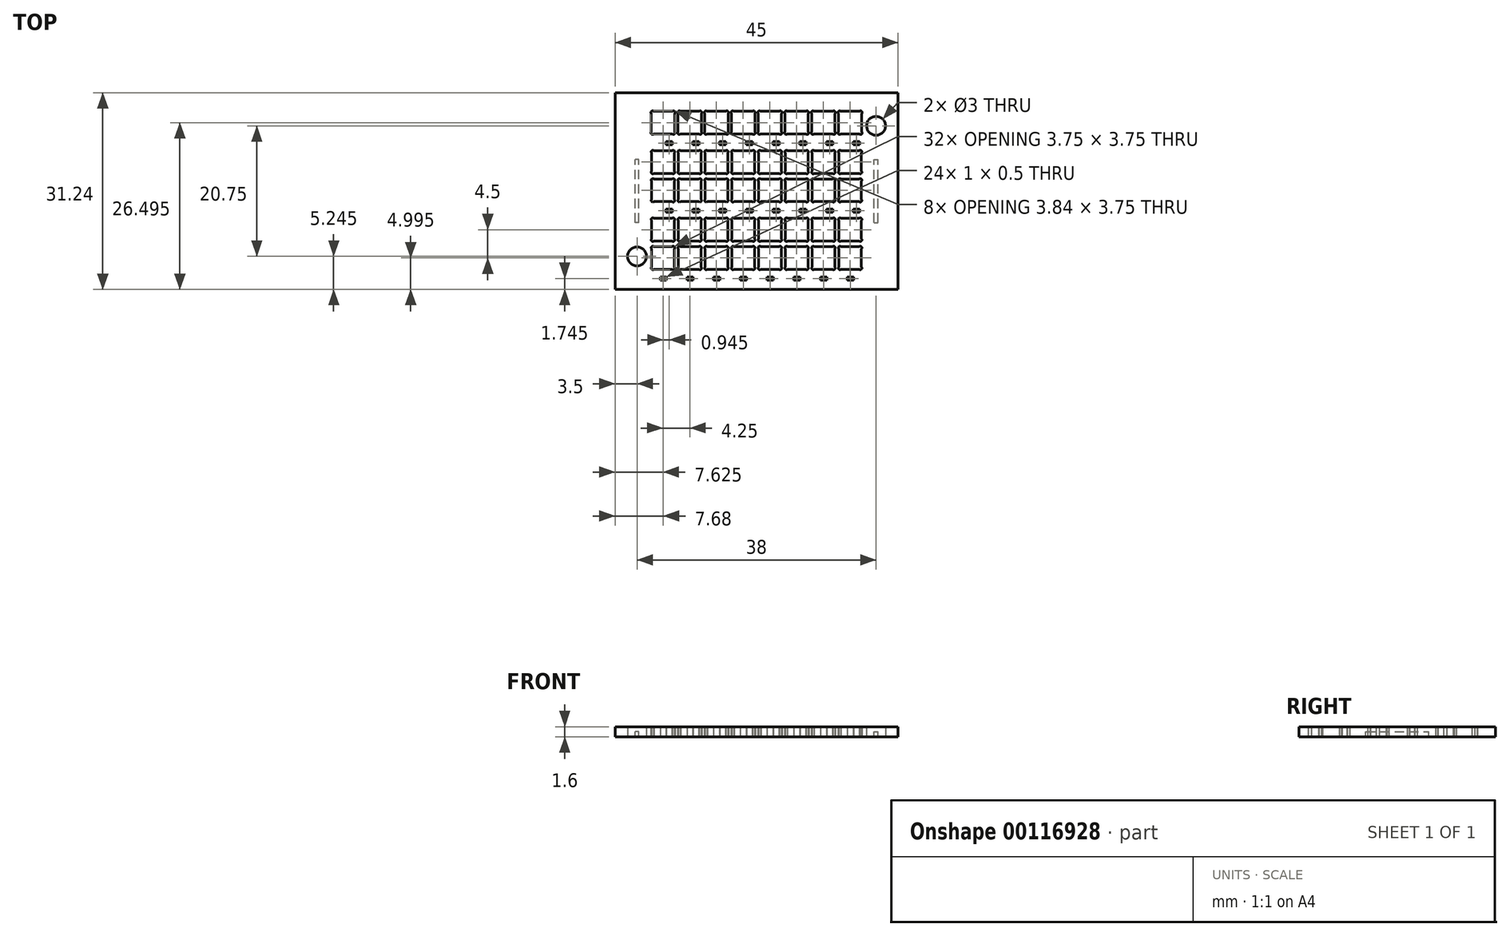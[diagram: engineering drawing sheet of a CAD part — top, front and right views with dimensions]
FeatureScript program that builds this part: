
annotation { "Feature Type Name" : "Feature", "Feature Type Description" : "" }
export const myFeature = defineFeature(function(context is Context, id is Id, definition is map)
    precondition{}
    {
        {
            var Q0;
            Q0=qCreatedBy(makeId("Top.planeOp"),FACE);
            var sketch = newSketch(context, id + "F0", { "sketchPlane" : qUnion([Q0])});
            skLineSegment(sketch, "E0.bottom", {"start": v(-13.38, 9.08) * mm, "end": v(-16.37, 9.08) * mm});
            skLineSegment(sketch, "E0.top", {"start": v(-13.38, 12.68) * mm, "end": v(-16.37, 12.68) * mm});
            skLineSegment(sketch, "E0.left", {"start": v(-13.03, 9.42) * mm, "end": v(-13.03, 12.33) * mm});
            skLineSegment(sketch, "E0.right", {"start": v(-16.73, 9.42) * mm, "end": v(-16.73, 12.33) * mm});
            skPoint(sketch, "E0.middle", {"position": v(-14.88, 10.88) * mm});
            skArc(sketch, "E1", {"start": v(-16.37, 12.68) * mm, "mid": v(-16.72, 12.68) * mm, "end": v(-16.73, 12.33) * mm});
            skLineSegment(sketch, "E2", {"start": v(-16.73, 12.68) * mm, "end": v(-14.88, 10.88) * mm, "construction": true});
            skLineSegment(sketch, "E3", {"start": v(-14.88, 12.68) * mm, "end": v(-14.88, 9.08) * mm, "construction": true});
            skLineSegment(sketch, "E4", {"start": v(-16.73, 10.88) * mm, "end": v(-13.03, 10.88) * mm, "construction": true});
            skArc(sketch, "E5.MirrorC", {"start": v(-16.37, 9.07) * mm, "mid": v(-16.72, 9.07) * mm, "end": v(-16.73, 9.42) * mm});
            skArc(sketch, "E6.MirrorC", {"start": v(-13.38, 12.68) * mm, "mid": v(-13.03, 12.68) * mm, "end": v(-13.03, 12.33) * mm});
            skArc(sketch, "E7.MirrorC", {"start": v(-13.38, 9.07) * mm, "mid": v(-13.03, 9.07) * mm, "end": v(-13.03, 9.42) * mm});
            skPoint(sketch, "E8.orphan", {"position": v(-13.03, 12.68) * mm});
            skPoint(sketch, "E9.orphan", {"position": v(-13.03, 9.07) * mm});
            skPoint(sketch, "E10.orphan", {"position": v(-16.73, 9.07) * mm});
            skLineSegment(sketch, "E11.1.0.0", {"start": v(-8.78, 9.42) * mm, "end": v(-8.78, 12.33) * mm});
            skArc(sketch, "E11.1.0.1", {"start": v(-9.13, 9.07) * mm, "mid": v(-8.78, 9.07) * mm, "end": v(-8.78, 9.42) * mm});
            skLineSegment(sketch, "E11.1.0.2", {"start": v(-9.13, 9.08) * mm, "end": v(-12.12, 9.08) * mm});
            skArc(sketch, "E11.1.0.3", {"start": v(-12.12, 9.07) * mm, "mid": v(-12.47, 9.07) * mm, "end": v(-12.48, 9.42) * mm});
            skLineSegment(sketch, "E11.1.0.4", {"start": v(-12.47, 9.42) * mm, "end": v(-12.47, 12.33) * mm});
            skArc(sketch, "E11.1.0.5", {"start": v(-12.12, 12.68) * mm, "mid": v(-12.47, 12.68) * mm, "end": v(-12.48, 12.33) * mm});
            skLineSegment(sketch, "E11.1.0.6", {"start": v(-9.13, 12.68) * mm, "end": v(-12.12, 12.68) * mm});
            skArc(sketch, "E11.1.0.7", {"start": v(-9.13, 12.68) * mm, "mid": v(-8.78, 12.68) * mm, "end": v(-8.78, 12.33) * mm});
            skLineSegment(sketch, "E11.2.0.0", {"start": v(-4.53, 9.42) * mm, "end": v(-4.53, 12.33) * mm});
            skArc(sketch, "E11.2.0.1", {"start": v(-4.88, 9.07) * mm, "mid": v(-4.53, 9.07) * mm, "end": v(-4.53, 9.42) * mm});
            skLineSegment(sketch, "E11.2.0.2", {"start": v(-4.88, 9.08) * mm, "end": v(-7.87, 9.08) * mm});
            skArc(sketch, "E11.2.0.3", {"start": v(-7.87, 9.07) * mm, "mid": v(-8.22, 9.07) * mm, "end": v(-8.23, 9.42) * mm});
            skLineSegment(sketch, "E11.2.0.4", {"start": v(-8.22, 9.42) * mm, "end": v(-8.22, 12.33) * mm});
            skArc(sketch, "E11.2.0.5", {"start": v(-7.87, 12.68) * mm, "mid": v(-8.22, 12.68) * mm, "end": v(-8.23, 12.33) * mm});
            skLineSegment(sketch, "E11.2.0.6", {"start": v(-4.88, 12.68) * mm, "end": v(-7.87, 12.68) * mm});
            skArc(sketch, "E11.2.0.7", {"start": v(-4.88, 12.68) * mm, "mid": v(-4.53, 12.68) * mm, "end": v(-4.53, 12.33) * mm});
            skLineSegment(sketch, "E11.3.0.0", {"start": v(-0.28, 9.42) * mm, "end": v(-0.28, 12.33) * mm});
            skArc(sketch, "E11.3.0.1", {"start": v(-0.63, 9.07) * mm, "mid": v(-0.28, 9.07) * mm, "end": v(-0.28, 9.42) * mm});
            skLineSegment(sketch, "E11.3.0.2", {"start": v(-0.63, 9.08) * mm, "end": v(-3.62, 9.08) * mm});
            skArc(sketch, "E11.3.0.3", {"start": v(-3.62, 9.07) * mm, "mid": v(-3.97, 9.07) * mm, "end": v(-3.98, 9.42) * mm});
            skLineSegment(sketch, "E11.3.0.4", {"start": v(-3.97, 9.42) * mm, "end": v(-3.97, 12.33) * mm});
            skArc(sketch, "E11.3.0.5", {"start": v(-3.62, 12.68) * mm, "mid": v(-3.97, 12.68) * mm, "end": v(-3.98, 12.33) * mm});
            skLineSegment(sketch, "E11.3.0.6", {"start": v(-0.63, 12.68) * mm, "end": v(-3.62, 12.68) * mm});
            skArc(sketch, "E11.3.0.7", {"start": v(-0.63, 12.68) * mm, "mid": v(-0.28, 12.68) * mm, "end": v(-0.28, 12.33) * mm});
            skLineSegment(sketch, "E11.4.0.0", {"start": v(3.97, 9.42) * mm, "end": v(3.97, 12.33) * mm});
            skArc(sketch, "E11.4.0.1", {"start": v(3.62, 9.07) * mm, "mid": v(3.97, 9.07) * mm, "end": v(3.97, 9.42) * mm});
            skLineSegment(sketch, "E11.4.0.2", {"start": v(3.62, 9.08) * mm, "end": v(0.63, 9.08) * mm});
            skArc(sketch, "E11.4.0.3", {"start": v(0.63, 9.07) * mm, "mid": v(0.28, 9.07) * mm, "end": v(0.27, 9.42) * mm});
            skLineSegment(sketch, "E11.4.0.4", {"start": v(0.28, 9.42) * mm, "end": v(0.28, 12.33) * mm});
            skArc(sketch, "E11.4.0.5", {"start": v(0.63, 12.68) * mm, "mid": v(0.28, 12.68) * mm, "end": v(0.27, 12.33) * mm});
            skLineSegment(sketch, "E11.4.0.6", {"start": v(3.62, 12.68) * mm, "end": v(0.63, 12.68) * mm});
            skArc(sketch, "E11.4.0.7", {"start": v(3.62, 12.68) * mm, "mid": v(3.97, 12.68) * mm, "end": v(3.97, 12.33) * mm});
            skLineSegment(sketch, "E11.5.0.0", {"start": v(8.22, 9.42) * mm, "end": v(8.22, 12.33) * mm});
            skArc(sketch, "E11.5.0.1", {"start": v(7.87, 9.07) * mm, "mid": v(8.22, 9.07) * mm, "end": v(8.22, 9.42) * mm});
            skLineSegment(sketch, "E11.5.0.2", {"start": v(7.87, 9.08) * mm, "end": v(4.88, 9.08) * mm});
            skArc(sketch, "E11.5.0.3", {"start": v(4.88, 9.07) * mm, "mid": v(4.53, 9.07) * mm, "end": v(4.52, 9.42) * mm});
            skLineSegment(sketch, "E11.5.0.4", {"start": v(4.53, 9.42) * mm, "end": v(4.53, 12.33) * mm});
            skArc(sketch, "E11.5.0.5", {"start": v(4.88, 12.68) * mm, "mid": v(4.53, 12.68) * mm, "end": v(4.52, 12.33) * mm});
            skLineSegment(sketch, "E11.5.0.6", {"start": v(7.87, 12.68) * mm, "end": v(4.88, 12.68) * mm});
            skArc(sketch, "E11.5.0.7", {"start": v(7.87, 12.68) * mm, "mid": v(8.22, 12.68) * mm, "end": v(8.22, 12.33) * mm});
            skLineSegment(sketch, "E11.6.0.0", {"start": v(12.47, 9.42) * mm, "end": v(12.47, 12.33) * mm});
            skArc(sketch, "E11.6.0.1", {"start": v(12.12, 9.07) * mm, "mid": v(12.47, 9.07) * mm, "end": v(12.47, 9.42) * mm});
            skLineSegment(sketch, "E11.6.0.2", {"start": v(12.12, 9.08) * mm, "end": v(9.13, 9.08) * mm});
            skArc(sketch, "E11.6.0.3", {"start": v(9.13, 9.07) * mm, "mid": v(8.78, 9.07) * mm, "end": v(8.77, 9.42) * mm});
            skLineSegment(sketch, "E11.6.0.4", {"start": v(8.78, 9.42) * mm, "end": v(8.78, 12.33) * mm});
            skArc(sketch, "E11.6.0.5", {"start": v(9.13, 12.68) * mm, "mid": v(8.78, 12.68) * mm, "end": v(8.77, 12.33) * mm});
            skLineSegment(sketch, "E11.6.0.6", {"start": v(12.12, 12.68) * mm, "end": v(9.13, 12.68) * mm});
            skArc(sketch, "E11.6.0.7", {"start": v(12.12, 12.68) * mm, "mid": v(12.47, 12.68) * mm, "end": v(12.47, 12.33) * mm});
            skLineSegment(sketch, "E11.7.0.0", {"start": v(16.73, 9.42) * mm, "end": v(16.73, 12.33) * mm});
            skArc(sketch, "E11.7.0.1", {"start": v(16.37, 9.07) * mm, "mid": v(16.72, 9.07) * mm, "end": v(16.73, 9.42) * mm});
            skLineSegment(sketch, "E11.7.0.2", {"start": v(16.37, 9.08) * mm, "end": v(13.38, 9.08) * mm});
            skArc(sketch, "E11.7.0.3", {"start": v(13.38, 9.08) * mm, "mid": v(13.03, 9.07) * mm, "end": v(13.02, 9.42) * mm});
            skLineSegment(sketch, "E11.7.0.4", {"start": v(13.03, 9.42) * mm, "end": v(13.03, 12.33) * mm});
            skArc(sketch, "E11.7.0.5", {"start": v(13.38, 12.68) * mm, "mid": v(13.03, 12.68) * mm, "end": v(13.02, 12.33) * mm});
            skLineSegment(sketch, "E11.7.0.6", {"start": v(16.37, 12.68) * mm, "end": v(13.38, 12.68) * mm});
            skArc(sketch, "E11.7.0.7", {"start": v(16.37, 12.68) * mm, "mid": v(16.72, 12.68) * mm, "end": v(16.73, 12.33) * mm});
            skLineSegment(sketch, "E11.direction1", {"start": v(-13.03, 9.42) * mm, "end": v(-8.78, 9.42) * mm, "construction": true});
            skLineSegment(sketch, "E12", {"start": v(-16.73, 10.87) * mm, "end": v(16.73, 10.88) * mm, "construction": true});
            skPoint(sketch, "E13", {"position": v(0, 10.87) * mm});
            skCircle(sketch, "E14", {"center": v(-19, 10.38) * mm, "radius": 1.5 * mm});
            skCircle(sketch, "E15.MirrorC", {"center": v(19, 10.38) * mm, "radius": 1.5 * mm});
            skCircle(sketch, "E16.MirrorC", {"center": v(-19, -10.38) * mm, "radius": 1.5 * mm});
            skCircle(sketch, "E17.MirrorC", {"center": v(19, -10.38) * mm, "radius": 1.5 * mm});
            skLineSegment(sketch, "E18.0.1.0", {"start": v(8.17, -1.32) * mm, "end": v(8.17, 1.57) * mm});
            skLineSegment(sketch, "E18.0.1.1", {"start": v(-0.68, -1.68) * mm, "end": v(-3.57, -1.68) * mm});
            skLineSegment(sketch, "E18.0.1.2", {"start": v(7.82, -1.68) * mm, "end": v(4.93, -1.68) * mm});
            skLineSegment(sketch, "E18.0.1.3", {"start": v(16.32, -1.68) * mm, "end": v(13.43, -1.68) * mm});
            skPoint(sketch, "E18.0.1.5", {"position": v(0, 0.12) * mm});
            skLineSegment(sketch, "E18.0.1.6", {"start": v(-4.93, -1.68) * mm, "end": v(-7.82, -1.68) * mm});
            skLineSegment(sketch, "E18.0.1.7", {"start": v(12.07, -1.68) * mm, "end": v(9.18, -1.68) * mm});
            skLineSegment(sketch, "E18.0.1.8", {"start": v(3.57, -1.68) * mm, "end": v(0.68, -1.68) * mm});
            skPoint(sketch, "E18.0.1.9", {"position": v(-13.07, 1.93) * mm});
            skLineSegment(sketch, "E18.0.1.10", {"start": v(4.57, -1.32) * mm, "end": v(4.57, 1.57) * mm});
            skLineSegment(sketch, "E18.0.1.11", {"start": v(13.07, -1.32) * mm, "end": v(13.07, 1.57) * mm});
            skLineSegment(sketch, "E18.0.1.12", {"start": v(-3.93, -1.32) * mm, "end": v(-3.93, 1.57) * mm});
            skLineSegment(sketch, "E18.0.1.13", {"start": v(-9.18, -1.68) * mm, "end": v(-12.07, -1.68) * mm});
            skLineSegment(sketch, "E18.0.1.14", {"start": v(-8.83, -1.32) * mm, "end": v(-8.83, 1.57) * mm});
            skLineSegment(sketch, "E18.0.1.15", {"start": v(8.82, -1.32) * mm, "end": v(8.82, 1.57) * mm});
            skLineSegment(sketch, "E18.0.1.16", {"start": v(-8.18, -1.32) * mm, "end": v(-8.18, 1.57) * mm});
            skPoint(sketch, "E18.0.1.17", {"position": v(-13.07, -1.68) * mm});
            skPoint(sketch, "E18.0.1.18", {"position": v(-16.68, -1.67) * mm});
            skLineSegment(sketch, "E18.0.1.19", {"start": v(-9.18, 1.92) * mm, "end": v(-12.07, 1.92) * mm});
            skLineSegment(sketch, "E18.0.1.20", {"start": v(16.32, 1.92) * mm, "end": v(13.43, 1.92) * mm});
            skLineSegment(sketch, "E18.0.1.21", {"start": v(7.82, 1.92) * mm, "end": v(4.93, 1.92) * mm});
            skLineSegment(sketch, "E18.0.1.22", {"start": v(-0.68, 1.92) * mm, "end": v(-3.57, 1.92) * mm});
            skLineSegment(sketch, "E18.0.1.23", {"start": v(12.07, 1.92) * mm, "end": v(9.18, 1.92) * mm});
            skLineSegment(sketch, "E18.0.1.24", {"start": v(3.57, 1.92) * mm, "end": v(0.68, 1.92) * mm});
            skLineSegment(sketch, "E18.0.1.25", {"start": v(-4.93, 1.92) * mm, "end": v(-7.82, 1.92) * mm});
            skPoint(sketch, "E18.0.1.26", {"position": v(-14.88, 0.13) * mm});
            skLineSegment(sketch, "E18.0.1.27", {"start": v(3.92, -1.32) * mm, "end": v(3.92, 1.57) * mm});
            skLineSegment(sketch, "E18.0.1.28", {"start": v(12.42, -1.32) * mm, "end": v(12.42, 1.57) * mm});
            skLineSegment(sketch, "E18.0.1.30", {"start": v(-4.58, -1.32) * mm, "end": v(-4.58, 1.57) * mm});
            skLineSegment(sketch, "E18.0.1.31", {"start": v(-0.33, -1.32) * mm, "end": v(-0.33, 1.57) * mm});
            skLineSegment(sketch, "E18.0.1.32", {"start": v(16.68, -1.32) * mm, "end": v(16.68, 1.57) * mm});
            skLineSegment(sketch, "E18.0.1.34", {"start": v(-12.43, -1.32) * mm, "end": v(-12.43, 1.57) * mm});
            skLineSegment(sketch, "E18.0.1.35", {"start": v(-13.43, -1.68) * mm, "end": v(-16.32, -1.68) * mm});
            skLineSegment(sketch, "E18.0.1.36", {"start": v(-13.08, -1.32) * mm, "end": v(-13.08, 1.57) * mm});
            skLineSegment(sketch, "E18.0.1.39", {"start": v(0.32, -1.32) * mm, "end": v(0.32, 1.57) * mm});
            skArc(sketch, "E18.0.1.40", {"start": v(3.57, -1.68) * mm, "mid": v(3.92, -1.68) * mm, "end": v(3.92, -1.32) * mm});
            skArc(sketch, "E18.0.1.41", {"start": v(12.07, 1.92) * mm, "mid": v(12.42, 1.92) * mm, "end": v(12.42, 1.57) * mm});
            skArc(sketch, "E18.0.1.42", {"start": v(16.32, -1.68) * mm, "mid": v(16.67, -1.68) * mm, "end": v(16.67, -1.32) * mm});
            skArc(sketch, "E18.0.1.43", {"start": v(7.82, -1.68) * mm, "mid": v(8.17, -1.68) * mm, "end": v(8.17, -1.32) * mm});
            skArc(sketch, "E18.0.1.44", {"start": v(13.43, -1.68) * mm, "mid": v(13.07, -1.68) * mm, "end": v(13.07, -1.32) * mm});
            skArc(sketch, "E18.0.1.45", {"start": v(-3.57, -1.68) * mm, "mid": v(-3.93, -1.67) * mm, "end": v(-3.93, -1.32) * mm});
            skArc(sketch, "E18.0.1.46", {"start": v(-4.93, 1.93) * mm, "mid": v(-4.57, 1.92) * mm, "end": v(-4.58, 1.57) * mm});
            skLineSegment(sketch, "E18.0.1.47", {"start": v(-13.43, 1.92) * mm, "end": v(-16.32, 1.92) * mm});
            skLineSegment(sketch, "E18.0.1.48", {"start": v(-16.68, -1.32) * mm, "end": v(-16.68, 1.57) * mm});
            skArc(sketch, "E18.0.1.50", {"start": v(0.68, 1.92) * mm, "mid": v(0.32, 1.92) * mm, "end": v(0.32, 1.57) * mm});
            skArc(sketch, "E18.0.1.51", {"start": v(-7.82, 1.93) * mm, "mid": v(-8.18, 1.92) * mm, "end": v(-8.18, 1.57) * mm});
            skArc(sketch, "E18.0.1.52", {"start": v(16.32, 1.92) * mm, "mid": v(16.67, 1.92) * mm, "end": v(16.67, 1.57) * mm});
            skArc(sketch, "E18.0.1.53", {"start": v(-4.93, -1.68) * mm, "mid": v(-4.57, -1.68) * mm, "end": v(-4.57, -1.32) * mm});
            skArc(sketch, "E18.0.1.54", {"start": v(12.07, -1.68) * mm, "mid": v(12.42, -1.68) * mm, "end": v(12.42, -1.32) * mm});
            skArc(sketch, "E18.0.1.55", {"start": v(-0.68, -1.68) * mm, "mid": v(-0.32, -1.67) * mm, "end": v(-0.32, -1.32) * mm});
            skArc(sketch, "E18.0.1.56", {"start": v(4.93, -1.68) * mm, "mid": v(4.57, -1.68) * mm, "end": v(4.57, -1.32) * mm});
            skArc(sketch, "E18.0.1.57", {"start": v(3.57, 1.92) * mm, "mid": v(3.93, 1.92) * mm, "end": v(3.92, 1.57) * mm});
            skArc(sketch, "E18.0.1.58", {"start": v(-7.82, -1.68) * mm, "mid": v(-8.18, -1.67) * mm, "end": v(-8.18, -1.32) * mm});
            skArc(sketch, "E18.0.1.59", {"start": v(9.18, -1.68) * mm, "mid": v(8.82, -1.68) * mm, "end": v(8.82, -1.32) * mm});
            skArc(sketch, "E18.0.1.60", {"start": v(0.68, -1.68) * mm, "mid": v(0.32, -1.68) * mm, "end": v(0.32, -1.32) * mm});
            skArc(sketch, "E18.0.1.61", {"start": v(-16.32, -1.68) * mm, "mid": v(-16.68, -1.67) * mm, "end": v(-16.68, -1.32) * mm});
            skArc(sketch, "E18.0.1.62", {"start": v(-9.18, -1.68) * mm, "mid": v(-8.82, -1.68) * mm, "end": v(-8.82, -1.32) * mm});
            skArc(sketch, "E18.0.1.63", {"start": v(7.82, 1.92) * mm, "mid": v(8.17, 1.92) * mm, "end": v(8.17, 1.57) * mm});
            skArc(sketch, "E18.0.1.64", {"start": v(-12.07, 1.93) * mm, "mid": v(-12.43, 1.92) * mm, "end": v(-12.43, 1.57) * mm});
            skArc(sketch, "E18.0.1.65", {"start": v(13.43, 1.92) * mm, "mid": v(13.07, 1.92) * mm, "end": v(13.07, 1.57) * mm});
            skArc(sketch, "E18.0.1.66", {"start": v(4.93, 1.92) * mm, "mid": v(4.57, 1.92) * mm, "end": v(4.57, 1.57) * mm});
            skArc(sketch, "E18.0.1.67", {"start": v(-3.57, 1.93) * mm, "mid": v(-3.93, 1.92) * mm, "end": v(-3.93, 1.57) * mm});
            skArc(sketch, "E18.0.1.68", {"start": v(9.18, 1.92) * mm, "mid": v(8.82, 1.92) * mm, "end": v(8.82, 1.57) * mm});
            skArc(sketch, "E18.0.1.69", {"start": v(-9.18, 1.93) * mm, "mid": v(-8.82, 1.92) * mm, "end": v(-8.82, 1.57) * mm});
            skArc(sketch, "E18.0.1.70", {"start": v(-12.07, -1.68) * mm, "mid": v(-12.43, -1.67) * mm, "end": v(-12.43, -1.32) * mm});
            skArc(sketch, "E18.0.1.71", {"start": v(-13.43, 1.93) * mm, "mid": v(-13.07, 1.92) * mm, "end": v(-13.07, 1.57) * mm});
            skArc(sketch, "E18.0.1.72", {"start": v(-13.43, -1.68) * mm, "mid": v(-13.07, -1.68) * mm, "end": v(-13.07, -1.32) * mm});
            skArc(sketch, "E18.0.1.73", {"start": v(-0.68, 1.93) * mm, "mid": v(-0.32, 1.92) * mm, "end": v(-0.33, 1.57) * mm});
            skArc(sketch, "E18.0.1.74", {"start": v(-16.32, 1.93) * mm, "mid": v(-16.68, 1.92) * mm, "end": v(-16.68, 1.57) * mm});
            skLineSegment(sketch, "E18.0.2.0", {"start": v(8.17, -12.07) * mm, "end": v(8.17, -9.18) * mm});
            skLineSegment(sketch, "E18.0.2.1", {"start": v(-0.68, -12.43) * mm, "end": v(-3.57, -12.43) * mm});
            skLineSegment(sketch, "E18.0.2.2", {"start": v(7.82, -12.43) * mm, "end": v(4.93, -12.43) * mm});
            skLineSegment(sketch, "E18.0.2.3", {"start": v(16.32, -12.43) * mm, "end": v(13.43, -12.43) * mm});
            skPoint(sketch, "E18.0.2.5", {"position": v(0, -10.63) * mm});
            skLineSegment(sketch, "E18.0.2.6", {"start": v(-4.93, -12.43) * mm, "end": v(-7.82, -12.43) * mm});
            skLineSegment(sketch, "E18.0.2.7", {"start": v(12.07, -12.43) * mm, "end": v(9.18, -12.43) * mm});
            skLineSegment(sketch, "E18.0.2.8", {"start": v(3.57, -12.43) * mm, "end": v(0.68, -12.43) * mm});
            skPoint(sketch, "E18.0.2.9", {"position": v(-13.07, -8.82) * mm});
            skLineSegment(sketch, "E18.0.2.10", {"start": v(4.57, -12.07) * mm, "end": v(4.57, -9.18) * mm});
            skLineSegment(sketch, "E18.0.2.11", {"start": v(13.07, -12.07) * mm, "end": v(13.07, -9.18) * mm});
            skLineSegment(sketch, "E18.0.2.12", {"start": v(-3.93, -12.07) * mm, "end": v(-3.93, -9.18) * mm});
            skLineSegment(sketch, "E18.0.2.13", {"start": v(-9.18, -12.43) * mm, "end": v(-12.07, -12.43) * mm});
            skLineSegment(sketch, "E18.0.2.14", {"start": v(-8.83, -12.07) * mm, "end": v(-8.83, -9.18) * mm});
            skLineSegment(sketch, "E18.0.2.15", {"start": v(8.82, -12.07) * mm, "end": v(8.82, -9.18) * mm});
            skLineSegment(sketch, "E18.0.2.16", {"start": v(-8.18, -12.07) * mm, "end": v(-8.18, -9.18) * mm});
            skPoint(sketch, "E18.0.2.17", {"position": v(-13.07, -12.43) * mm});
            skPoint(sketch, "E18.0.2.18", {"position": v(-16.68, -12.43) * mm});
            skLineSegment(sketch, "E18.0.2.19", {"start": v(-9.18, -8.83) * mm, "end": v(-12.07, -8.83) * mm});
            skLineSegment(sketch, "E18.0.2.20", {"start": v(16.32, -8.83) * mm, "end": v(13.43, -8.83) * mm});
            skLineSegment(sketch, "E18.0.2.21", {"start": v(7.82, -8.83) * mm, "end": v(4.93, -8.83) * mm});
            skLineSegment(sketch, "E18.0.2.22", {"start": v(-0.68, -8.83) * mm, "end": v(-3.57, -8.83) * mm});
            skLineSegment(sketch, "E18.0.2.23", {"start": v(12.07, -8.83) * mm, "end": v(9.18, -8.83) * mm});
            skLineSegment(sketch, "E18.0.2.24", {"start": v(3.57, -8.83) * mm, "end": v(0.68, -8.83) * mm});
            skLineSegment(sketch, "E18.0.2.25", {"start": v(-4.93, -8.83) * mm, "end": v(-7.82, -8.83) * mm});
            skPoint(sketch, "E18.0.2.26", {"position": v(-14.82, -9.25) * mm});
            skLineSegment(sketch, "E18.0.2.27", {"start": v(3.92, -12.07) * mm, "end": v(3.92, -9.18) * mm});
            skLineSegment(sketch, "E18.0.2.28", {"start": v(12.42, -12.07) * mm, "end": v(12.42, -9.18) * mm});
            skLineSegment(sketch, "E18.0.2.30", {"start": v(-4.58, -12.07) * mm, "end": v(-4.58, -9.18) * mm});
            skLineSegment(sketch, "E18.0.2.31", {"start": v(-0.33, -12.07) * mm, "end": v(-0.33, -9.18) * mm});
            skLineSegment(sketch, "E18.0.2.32", {"start": v(16.68, -12.07) * mm, "end": v(16.68, -9.18) * mm});
            skLineSegment(sketch, "E18.0.2.34", {"start": v(-12.43, -12.07) * mm, "end": v(-12.43, -9.18) * mm});
            skLineSegment(sketch, "E18.0.2.35", {"start": v(-13.43, -12.43) * mm, "end": v(-16.32, -12.43) * mm});
            skLineSegment(sketch, "E18.0.2.36", {"start": v(-13.08, -12.07) * mm, "end": v(-13.08, -9.18) * mm});
            skLineSegment(sketch, "E18.0.2.39", {"start": v(0.32, -12.07) * mm, "end": v(0.32, -9.18) * mm});
            skArc(sketch, "E18.0.2.40", {"start": v(3.57, -12.43) * mm, "mid": v(3.92, -12.43) * mm, "end": v(3.92, -12.07) * mm});
            skArc(sketch, "E18.0.2.41", {"start": v(12.07, -8.83) * mm, "mid": v(12.42, -8.83) * mm, "end": v(12.42, -9.18) * mm});
            skArc(sketch, "E18.0.2.42", {"start": v(16.32, -12.43) * mm, "mid": v(16.67, -12.43) * mm, "end": v(16.67, -12.07) * mm});
            skArc(sketch, "E18.0.2.43", {"start": v(7.82, -12.43) * mm, "mid": v(8.17, -12.43) * mm, "end": v(8.17, -12.07) * mm});
            skArc(sketch, "E18.0.2.44", {"start": v(13.43, -12.43) * mm, "mid": v(13.07, -12.43) * mm, "end": v(13.07, -12.07) * mm});
            skArc(sketch, "E18.0.2.45", {"start": v(-3.57, -12.43) * mm, "mid": v(-3.93, -12.43) * mm, "end": v(-3.93, -12.07) * mm});
            skArc(sketch, "E18.0.2.46", {"start": v(-4.93, -8.82) * mm, "mid": v(-4.57, -8.83) * mm, "end": v(-4.58, -9.18) * mm});
            skLineSegment(sketch, "E18.0.2.47", {"start": v(-13.43, -8.83) * mm, "end": v(-16.32, -8.83) * mm});
            skLineSegment(sketch, "E18.0.2.48", {"start": v(-16.68, -12.07) * mm, "end": v(-16.68, -9.18) * mm});
            skLineSegment(sketch, "E18.0.2.49", {"start": v(-16.62, -7.45) * mm, "end": v(-14.82, -9.25) * mm, "construction": true});
            skArc(sketch, "E18.0.2.50", {"start": v(0.68, -8.83) * mm, "mid": v(0.32, -8.83) * mm, "end": v(0.32, -9.18) * mm});
            skArc(sketch, "E18.0.2.51", {"start": v(-7.82, -8.82) * mm, "mid": v(-8.18, -8.83) * mm, "end": v(-8.18, -9.18) * mm});
            skArc(sketch, "E18.0.2.52", {"start": v(16.32, -8.83) * mm, "mid": v(16.67, -8.83) * mm, "end": v(16.67, -9.18) * mm});
            skArc(sketch, "E18.0.2.53", {"start": v(-4.93, -12.43) * mm, "mid": v(-4.57, -12.43) * mm, "end": v(-4.57, -12.07) * mm});
            skArc(sketch, "E18.0.2.54", {"start": v(12.07, -12.43) * mm, "mid": v(12.42, -12.43) * mm, "end": v(12.42, -12.07) * mm});
            skArc(sketch, "E18.0.2.55", {"start": v(-0.68, -12.43) * mm, "mid": v(-0.32, -12.43) * mm, "end": v(-0.32, -12.07) * mm});
            skArc(sketch, "E18.0.2.56", {"start": v(4.93, -12.43) * mm, "mid": v(4.57, -12.43) * mm, "end": v(4.57, -12.07) * mm});
            skArc(sketch, "E18.0.2.57", {"start": v(3.57, -8.83) * mm, "mid": v(3.93, -8.83) * mm, "end": v(3.92, -9.18) * mm});
            skArc(sketch, "E18.0.2.58", {"start": v(-7.82, -12.43) * mm, "mid": v(-8.18, -12.43) * mm, "end": v(-8.18, -12.07) * mm});
            skArc(sketch, "E18.0.2.59", {"start": v(9.18, -12.43) * mm, "mid": v(8.82, -12.43) * mm, "end": v(8.82, -12.07) * mm});
            skArc(sketch, "E18.0.2.60", {"start": v(0.68, -12.43) * mm, "mid": v(0.32, -12.43) * mm, "end": v(0.32, -12.07) * mm});
            skArc(sketch, "E18.0.2.61", {"start": v(-16.32, -12.43) * mm, "mid": v(-16.68, -12.43) * mm, "end": v(-16.68, -12.07) * mm});
            skArc(sketch, "E18.0.2.62", {"start": v(-9.18, -12.43) * mm, "mid": v(-8.82, -12.43) * mm, "end": v(-8.82, -12.07) * mm});
            skArc(sketch, "E18.0.2.63", {"start": v(7.82, -8.83) * mm, "mid": v(8.17, -8.83) * mm, "end": v(8.17, -9.18) * mm});
            skArc(sketch, "E18.0.2.64", {"start": v(-12.07, -8.82) * mm, "mid": v(-12.43, -8.83) * mm, "end": v(-12.43, -9.18) * mm});
            skArc(sketch, "E18.0.2.65", {"start": v(13.43, -8.83) * mm, "mid": v(13.07, -8.83) * mm, "end": v(13.07, -9.18) * mm});
            skArc(sketch, "E18.0.2.66", {"start": v(4.93, -8.83) * mm, "mid": v(4.57, -8.83) * mm, "end": v(4.57, -9.18) * mm});
            skArc(sketch, "E18.0.2.67", {"start": v(-3.57, -8.82) * mm, "mid": v(-3.93, -8.83) * mm, "end": v(-3.93, -9.18) * mm});
            skArc(sketch, "E18.0.2.68", {"start": v(9.18, -8.83) * mm, "mid": v(8.82, -8.83) * mm, "end": v(8.82, -9.18) * mm});
            skArc(sketch, "E18.0.2.69", {"start": v(-9.18, -8.82) * mm, "mid": v(-8.82, -8.83) * mm, "end": v(-8.82, -9.18) * mm});
            skArc(sketch, "E18.0.2.70", {"start": v(-12.07, -12.43) * mm, "mid": v(-12.43, -12.43) * mm, "end": v(-12.43, -12.07) * mm});
            skArc(sketch, "E18.0.2.71", {"start": v(-13.43, -8.82) * mm, "mid": v(-13.07, -8.83) * mm, "end": v(-13.07, -9.18) * mm});
            skArc(sketch, "E18.0.2.72", {"start": v(-13.43, -12.43) * mm, "mid": v(-13.07, -12.43) * mm, "end": v(-13.07, -12.07) * mm});
            skArc(sketch, "E18.0.2.73", {"start": v(-0.68, -8.82) * mm, "mid": v(-0.32, -8.83) * mm, "end": v(-0.33, -9.18) * mm});
            skArc(sketch, "E18.0.2.74", {"start": v(-16.32, -8.82) * mm, "mid": v(-16.68, -8.83) * mm, "end": v(-16.68, -9.18) * mm});
            skLineSegment(sketch, "E18.direction1", {"start": v(-16.73, 9.08) * mm, "end": v(8.34, 9.08) * mm, "construction": true});
            skPoint(sketch, "E19.0.1.0", {"position": v(-13.07, 2.82) * mm});
            skLineSegment(sketch, "E19.0.1.1", {"start": v(-0.68, 2.82) * mm, "end": v(-3.57, 2.82) * mm});
            skLineSegment(sketch, "E19.0.1.2", {"start": v(-12.43, -7.57) * mm, "end": v(-12.43, -4.68) * mm});
            skLineSegment(sketch, "E19.0.1.3", {"start": v(7.82, 6.42) * mm, "end": v(4.93, 6.42) * mm});
            skLineSegment(sketch, "E19.0.1.4", {"start": v(-8.83, -7.57) * mm, "end": v(-8.83, -4.68) * mm});
            skLineSegment(sketch, "E19.0.1.5", {"start": v(16.32, -7.93) * mm, "end": v(13.43, -7.93) * mm});
            skPoint(sketch, "E19.0.1.6", {"position": v(-13.07, 6.43) * mm});
            skLineSegment(sketch, "E19.0.1.7", {"start": v(-9.18, -7.93) * mm, "end": v(-12.07, -7.93) * mm});
            skLineSegment(sketch, "E19.0.1.8", {"start": v(16.32, 6.42) * mm, "end": v(13.43, 6.42) * mm});
            skLineSegment(sketch, "E19.0.1.9", {"start": v(8.17, 3.18) * mm, "end": v(8.17, 6.07) * mm});
            skPoint(sketch, "E19.0.1.10", {"position": v(-14.88, 4.63) * mm});
            skPoint(sketch, "E19.0.1.11", {"position": v(0, 4.62) * mm});
            skLineSegment(sketch, "E19.0.1.12", {"start": v(13.07, -7.57) * mm, "end": v(13.07, -4.68) * mm});
            skPoint(sketch, "E19.0.1.14", {"position": v(-16.68, -7.92) * mm});
            skLineSegment(sketch, "E19.0.1.15", {"start": v(-4.58, -7.57) * mm, "end": v(-4.58, -4.68) * mm});
            skLineSegment(sketch, "E19.0.1.16", {"start": v(3.92, -7.57) * mm, "end": v(3.92, -4.68) * mm});
            skLineSegment(sketch, "E19.0.1.17", {"start": v(4.57, 3.18) * mm, "end": v(4.57, 6.07) * mm});
            skLineSegment(sketch, "E19.0.1.18", {"start": v(3.57, 6.42) * mm, "end": v(0.68, 6.42) * mm});
            skLineSegment(sketch, "E19.0.1.19", {"start": v(12.07, -4.33) * mm, "end": v(9.18, -4.33) * mm});
            skLineSegment(sketch, "E19.0.1.20", {"start": v(-9.18, -4.33) * mm, "end": v(-12.07, -4.33) * mm});
            skLineSegment(sketch, "E19.0.1.21", {"start": v(3.57, 2.82) * mm, "end": v(0.68, 2.82) * mm});
            skLineSegment(sketch, "E19.0.1.22", {"start": v(-0.68, 6.42) * mm, "end": v(-3.57, 6.42) * mm});
            skLineSegment(sketch, "E19.0.1.23", {"start": v(7.82, 2.82) * mm, "end": v(4.93, 2.82) * mm});
            skLineSegment(sketch, "E19.0.1.24", {"start": v(8.82, -7.57) * mm, "end": v(8.82, -4.68) * mm});
            skPoint(sketch, "E19.0.1.27", {"position": v(-16.68, 2.83) * mm});
            skLineSegment(sketch, "E19.0.1.28", {"start": v(12.07, 6.42) * mm, "end": v(9.18, 6.42) * mm});
            skLineSegment(sketch, "E19.0.1.29", {"start": v(16.32, 2.82) * mm, "end": v(13.43, 2.82) * mm});
            skLineSegment(sketch, "E19.0.1.30", {"start": v(-8.18, -7.57) * mm, "end": v(-8.18, -4.68) * mm});
            skLineSegment(sketch, "E19.0.1.31", {"start": v(-12.43, 3.18) * mm, "end": v(-12.43, 6.07) * mm});
            skLineSegment(sketch, "E19.0.1.32", {"start": v(13.07, 3.18) * mm, "end": v(13.07, 6.07) * mm});
            skLineSegment(sketch, "E19.0.1.33", {"start": v(-4.93, 2.82) * mm, "end": v(-7.82, 2.82) * mm});
            skLineSegment(sketch, "E19.0.1.34", {"start": v(-8.83, 3.18) * mm, "end": v(-8.83, 6.07) * mm});
            skLineSegment(sketch, "E19.0.1.35", {"start": v(8.82, 3.18) * mm, "end": v(8.82, 6.07) * mm});
            skLineSegment(sketch, "E19.0.1.36", {"start": v(8.17, -7.57) * mm, "end": v(8.17, -4.68) * mm});
            skPoint(sketch, "E19.0.1.37", {"position": v(0, -6.13) * mm});
            skLineSegment(sketch, "E19.0.1.38", {"start": v(-4.93, 6.42) * mm, "end": v(-7.82, 6.42) * mm});
            skLineSegment(sketch, "E19.0.1.39", {"start": v(16.32, -4.33) * mm, "end": v(13.43, -4.33) * mm});
            skLineSegment(sketch, "E19.0.1.40", {"start": v(3.57, -7.93) * mm, "end": v(0.68, -7.93) * mm});
            skLineSegment(sketch, "E19.0.1.41", {"start": v(4.57, -7.57) * mm, "end": v(4.57, -4.68) * mm});
            skLineSegment(sketch, "E19.0.1.42", {"start": v(12.42, -7.57) * mm, "end": v(12.42, -4.68) * mm});
            skLineSegment(sketch, "E19.0.1.44", {"start": v(-9.18, 6.42) * mm, "end": v(-12.07, 6.42) * mm});
            skLineSegment(sketch, "E19.0.1.45", {"start": v(-3.93, -7.57) * mm, "end": v(-3.93, -4.68) * mm});
            skLineSegment(sketch, "E19.0.1.46", {"start": v(-8.18, 3.18) * mm, "end": v(-8.18, 6.07) * mm});
            skLineSegment(sketch, "E19.0.1.47", {"start": v(12.07, -7.93) * mm, "end": v(9.18, -7.93) * mm});
            skPoint(sketch, "E19.0.1.48", {"position": v(-14.82, -4.75) * mm});
            skLineSegment(sketch, "E19.0.1.49", {"start": v(-4.58, 3.18) * mm, "end": v(-4.58, 6.07) * mm});
            skLineSegment(sketch, "E19.0.1.50", {"start": v(3.57, -4.33) * mm, "end": v(0.68, -4.33) * mm});
            skLineSegment(sketch, "E19.0.1.51", {"start": v(12.07, 2.82) * mm, "end": v(9.18, 2.82) * mm});
            skLineSegment(sketch, "E19.0.1.52", {"start": v(-3.93, 3.18) * mm, "end": v(-3.93, 6.07) * mm});
            skLineSegment(sketch, "E19.0.1.53", {"start": v(-4.93, -7.93) * mm, "end": v(-7.82, -7.93) * mm});
            skLineSegment(sketch, "E19.0.1.54", {"start": v(-4.93, -4.33) * mm, "end": v(-7.82, -4.33) * mm});
            skLineSegment(sketch, "E19.0.1.55", {"start": v(-0.68, -7.93) * mm, "end": v(-3.57, -7.93) * mm});
            skPoint(sketch, "E19.0.1.56", {"position": v(-13.07, -4.32) * mm});
            skLineSegment(sketch, "E19.0.1.57", {"start": v(3.92, 3.18) * mm, "end": v(3.92, 6.07) * mm});
            skLineSegment(sketch, "E19.0.1.58", {"start": v(7.82, -4.33) * mm, "end": v(4.93, -4.33) * mm});
            skLineSegment(sketch, "E19.0.1.59", {"start": v(-9.18, 2.82) * mm, "end": v(-12.07, 2.82) * mm});
            skLineSegment(sketch, "E19.0.1.60", {"start": v(7.82, -7.93) * mm, "end": v(4.93, -7.93) * mm});
            skLineSegment(sketch, "E19.0.1.61", {"start": v(12.42, 3.18) * mm, "end": v(12.42, 6.07) * mm});
            skPoint(sketch, "E19.0.1.62", {"position": v(-13.07, -7.93) * mm});
            skLineSegment(sketch, "E19.0.1.63", {"start": v(-0.68, -4.33) * mm, "end": v(-3.57, -4.33) * mm});
            skLineSegment(sketch, "E19.0.1.64", {"start": v(0.32, 3.18) * mm, "end": v(0.32, 6.07) * mm});
            skLineSegment(sketch, "E19.0.1.65", {"start": v(-0.33, -7.57) * mm, "end": v(-0.33, -4.68) * mm});
            skLineSegment(sketch, "E19.0.1.66", {"start": v(16.68, -7.57) * mm, "end": v(16.68, -4.68) * mm});
            skLineSegment(sketch, "E19.0.1.68", {"start": v(-13.43, -4.33) * mm, "end": v(-16.32, -4.33) * mm});
            skLineSegment(sketch, "E19.0.1.70", {"start": v(-13.43, -7.93) * mm, "end": v(-16.32, -7.93) * mm});
            skLineSegment(sketch, "E19.0.1.71", {"start": v(-13.08, -7.57) * mm, "end": v(-13.08, -4.68) * mm});
            skLineSegment(sketch, "E19.0.1.73", {"start": v(-13.43, 2.82) * mm, "end": v(-16.32, 2.82) * mm});
            skLineSegment(sketch, "E19.0.1.75", {"start": v(-13.08, 3.18) * mm, "end": v(-13.08, 6.07) * mm});
            skLineSegment(sketch, "E19.0.1.76", {"start": v(16.68, 3.18) * mm, "end": v(16.68, 6.07) * mm});
            skLineSegment(sketch, "E19.0.1.77", {"start": v(-13.43, 6.42) * mm, "end": v(-16.32, 6.42) * mm});
            skLineSegment(sketch, "E19.0.1.78", {"start": v(-0.33, 3.18) * mm, "end": v(-0.33, 6.07) * mm});
            skLineSegment(sketch, "E19.0.1.79", {"start": v(0.32, -7.57) * mm, "end": v(0.32, -4.68) * mm});
            skArc(sketch, "E19.0.1.80", {"start": v(4.93, -4.33) * mm, "mid": v(4.57, -4.33) * mm, "end": v(4.57, -4.68) * mm});
            skLineSegment(sketch, "E19.0.1.81", {"start": v(-16.68, -7.57) * mm, "end": v(-16.68, -4.68) * mm});
            skArc(sketch, "E19.0.1.82", {"start": v(-9.18, 6.43) * mm, "mid": v(-8.82, 6.42) * mm, "end": v(-8.82, 6.07) * mm});
            skArc(sketch, "E19.0.1.83", {"start": v(-4.93, 2.82) * mm, "mid": v(-4.57, 2.83) * mm, "end": v(-4.57, 3.18) * mm});
            skArc(sketch, "E19.0.1.84", {"start": v(13.43, -4.33) * mm, "mid": v(13.07, -4.33) * mm, "end": v(13.07, -4.68) * mm});
            skArc(sketch, "E19.0.1.86", {"start": v(12.07, 2.82) * mm, "mid": v(12.42, 2.82) * mm, "end": v(12.42, 3.18) * mm});
            skArc(sketch, "E19.0.1.87", {"start": v(3.57, 2.82) * mm, "mid": v(3.92, 2.82) * mm, "end": v(3.92, 3.18) * mm});
            skArc(sketch, "E19.0.1.88", {"start": v(-4.93, 6.43) * mm, "mid": v(-4.57, 6.42) * mm, "end": v(-4.58, 6.07) * mm});
            skArc(sketch, "E19.0.1.89", {"start": v(4.93, 2.82) * mm, "mid": v(4.57, 2.82) * mm, "end": v(4.57, 3.18) * mm});
            skArc(sketch, "E19.0.1.90", {"start": v(16.32, 2.82) * mm, "mid": v(16.67, 2.82) * mm, "end": v(16.67, 3.18) * mm});
            skArc(sketch, "E19.0.1.91", {"start": v(-4.93, -7.93) * mm, "mid": v(-4.57, -7.92) * mm, "end": v(-4.57, -7.57) * mm});
            skArc(sketch, "E19.0.1.92", {"start": v(3.57, -4.33) * mm, "mid": v(3.93, -4.33) * mm, "end": v(3.92, -4.68) * mm});
            skArc(sketch, "E19.0.1.93", {"start": v(12.07, 6.42) * mm, "mid": v(12.42, 6.42) * mm, "end": v(12.42, 6.07) * mm});
            skArc(sketch, "E19.0.1.94", {"start": v(-3.57, -7.93) * mm, "mid": v(-3.93, -7.92) * mm, "end": v(-3.93, -7.57) * mm});
            skArc(sketch, "E19.0.1.95", {"start": v(9.18, -4.33) * mm, "mid": v(8.82, -4.33) * mm, "end": v(8.82, -4.68) * mm});
            skArc(sketch, "E19.0.1.96", {"start": v(9.18, 2.82) * mm, "mid": v(8.82, 2.82) * mm, "end": v(8.82, 3.18) * mm});
            skArc(sketch, "E19.0.1.97", {"start": v(7.82, 2.82) * mm, "mid": v(8.17, 2.82) * mm, "end": v(8.17, 3.18) * mm});
            skArc(sketch, "E19.0.1.98", {"start": v(-12.07, -7.93) * mm, "mid": v(-12.43, -7.92) * mm, "end": v(-12.43, -7.57) * mm});
            skArc(sketch, "E19.0.1.99", {"start": v(12.07, -7.93) * mm, "mid": v(12.42, -7.93) * mm, "end": v(12.42, -7.57) * mm});
            skArc(sketch, "E19.0.1.100", {"start": v(-3.57, 6.43) * mm, "mid": v(-3.93, 6.42) * mm, "end": v(-3.93, 6.07) * mm});
            skArc(sketch, "E19.0.1.101", {"start": v(-7.82, 6.43) * mm, "mid": v(-8.18, 6.42) * mm, "end": v(-8.18, 6.07) * mm});
            skArc(sketch, "E19.0.1.102", {"start": v(16.32, 6.42) * mm, "mid": v(16.67, 6.42) * mm, "end": v(16.67, 6.07) * mm});
            skLineSegment(sketch, "E19.0.1.104", {"start": v(-16.68, 3.18) * mm, "end": v(-16.68, 6.07) * mm});
            skArc(sketch, "E19.0.1.105", {"start": v(0.68, 2.82) * mm, "mid": v(0.32, 2.82) * mm, "end": v(0.32, 3.18) * mm});
            skArc(sketch, "E19.0.1.106", {"start": v(13.43, 2.82) * mm, "mid": v(13.07, 2.82) * mm, "end": v(13.07, 3.18) * mm});
            skArc(sketch, "E19.0.1.107", {"start": v(-16.32, 6.43) * mm, "mid": v(-16.68, 6.42) * mm, "end": v(-16.68, 6.07) * mm});
            skArc(sketch, "E19.0.1.108", {"start": v(-13.43, 6.43) * mm, "mid": v(-13.07, 6.42) * mm, "end": v(-13.07, 6.07) * mm});
            skArc(sketch, "E19.0.1.109", {"start": v(0.68, -4.33) * mm, "mid": v(0.32, -4.33) * mm, "end": v(0.32, -4.68) * mm});
            skArc(sketch, "E19.0.1.110", {"start": v(-0.68, 2.82) * mm, "mid": v(-0.32, 2.83) * mm, "end": v(-0.32, 3.18) * mm});
            skArc(sketch, "E19.0.1.111", {"start": v(-12.07, 2.82) * mm, "mid": v(-12.43, 2.83) * mm, "end": v(-12.43, 3.18) * mm});
            skArc(sketch, "E19.0.1.112", {"start": v(13.43, -7.93) * mm, "mid": v(13.07, -7.93) * mm, "end": v(13.07, -7.57) * mm});
            skArc(sketch, "E19.0.1.113", {"start": v(7.82, -4.33) * mm, "mid": v(8.17, -4.33) * mm, "end": v(8.17, -4.68) * mm});
            skArc(sketch, "E19.0.1.114", {"start": v(9.18, 6.42) * mm, "mid": v(8.82, 6.42) * mm, "end": v(8.82, 6.07) * mm});
            skArc(sketch, "E19.0.1.115", {"start": v(-9.18, 2.82) * mm, "mid": v(-8.82, 2.83) * mm, "end": v(-8.82, 3.18) * mm});
            skArc(sketch, "E19.0.1.116", {"start": v(-7.82, 2.82) * mm, "mid": v(-8.18, 2.83) * mm, "end": v(-8.18, 3.18) * mm});
            skArc(sketch, "E19.0.1.117", {"start": v(-9.18, -4.32) * mm, "mid": v(-8.82, -4.33) * mm, "end": v(-8.82, -4.68) * mm});
            skArc(sketch, "E19.0.1.118", {"start": v(12.07, -4.33) * mm, "mid": v(12.42, -4.33) * mm, "end": v(12.42, -4.68) * mm});
            skArc(sketch, "E19.0.1.119", {"start": v(-0.68, -4.32) * mm, "mid": v(-0.32, -4.33) * mm, "end": v(-0.33, -4.68) * mm});
            skArc(sketch, "E19.0.1.120", {"start": v(-7.82, -4.32) * mm, "mid": v(-8.18, -4.33) * mm, "end": v(-8.18, -4.68) * mm});
            skArc(sketch, "E19.0.1.121", {"start": v(-13.43, 2.82) * mm, "mid": v(-13.07, 2.83) * mm, "end": v(-13.07, 3.18) * mm});
            skArc(sketch, "E19.0.1.122", {"start": v(-3.57, -4.32) * mm, "mid": v(-3.93, -4.33) * mm, "end": v(-3.93, -4.68) * mm});
            skArc(sketch, "E19.0.1.123", {"start": v(3.57, 6.42) * mm, "mid": v(3.93, 6.42) * mm, "end": v(3.92, 6.07) * mm});
            skArc(sketch, "E19.0.1.124", {"start": v(16.32, -4.33) * mm, "mid": v(16.67, -4.33) * mm, "end": v(16.67, -4.68) * mm});
            skArc(sketch, "E19.0.1.125", {"start": v(-0.68, 6.43) * mm, "mid": v(-0.32, 6.42) * mm, "end": v(-0.33, 6.07) * mm});
            skArc(sketch, "E19.0.1.126", {"start": v(0.68, 6.42) * mm, "mid": v(0.32, 6.42) * mm, "end": v(0.32, 6.07) * mm});
            skArc(sketch, "E19.0.1.127", {"start": v(4.93, 6.42) * mm, "mid": v(4.57, 6.42) * mm, "end": v(4.57, 6.07) * mm});
            skArc(sketch, "E19.0.1.128", {"start": v(-9.18, -7.93) * mm, "mid": v(-8.82, -7.92) * mm, "end": v(-8.82, -7.57) * mm});
            skArc(sketch, "E19.0.1.129", {"start": v(-4.93, -4.32) * mm, "mid": v(-4.57, -4.33) * mm, "end": v(-4.58, -4.68) * mm});
            skArc(sketch, "E19.0.1.130", {"start": v(-12.07, -4.32) * mm, "mid": v(-12.43, -4.33) * mm, "end": v(-12.43, -4.68) * mm});
            skArc(sketch, "E19.0.1.131", {"start": v(0.68, -7.93) * mm, "mid": v(0.32, -7.93) * mm, "end": v(0.32, -7.57) * mm});
            skArc(sketch, "E19.0.1.132", {"start": v(13.43, 6.42) * mm, "mid": v(13.07, 6.42) * mm, "end": v(13.07, 6.07) * mm});
            skArc(sketch, "E19.0.1.133", {"start": v(7.82, 6.42) * mm, "mid": v(8.17, 6.42) * mm, "end": v(8.17, 6.07) * mm});
            skArc(sketch, "E19.0.1.134", {"start": v(-7.82, -7.93) * mm, "mid": v(-8.18, -7.92) * mm, "end": v(-8.18, -7.57) * mm});
            skArc(sketch, "E19.0.1.135", {"start": v(-16.32, -4.32) * mm, "mid": v(-16.68, -4.33) * mm, "end": v(-16.68, -4.68) * mm});
            skArc(sketch, "E19.0.1.136", {"start": v(16.32, -7.93) * mm, "mid": v(16.67, -7.93) * mm, "end": v(16.67, -7.57) * mm});
            skArc(sketch, "E19.0.1.137", {"start": v(-12.07, 6.43) * mm, "mid": v(-12.43, 6.42) * mm, "end": v(-12.43, 6.07) * mm});
            skArc(sketch, "E19.0.1.138", {"start": v(9.18, -7.93) * mm, "mid": v(8.82, -7.93) * mm, "end": v(8.82, -7.57) * mm});
            skArc(sketch, "E19.0.1.139", {"start": v(7.82, -7.93) * mm, "mid": v(8.17, -7.93) * mm, "end": v(8.17, -7.57) * mm});
            skArc(sketch, "E19.0.1.140", {"start": v(-0.68, -7.93) * mm, "mid": v(-0.32, -7.92) * mm, "end": v(-0.32, -7.57) * mm});
            skArc(sketch, "E19.0.1.141", {"start": v(-16.32, 2.82) * mm, "mid": v(-16.68, 2.83) * mm, "end": v(-16.68, 3.18) * mm});
            skArc(sketch, "E19.0.1.142", {"start": v(-3.57, 2.82) * mm, "mid": v(-3.93, 2.83) * mm, "end": v(-3.93, 3.18) * mm});
            skArc(sketch, "E19.0.1.143", {"start": v(4.93, -7.93) * mm, "mid": v(4.57, -7.93) * mm, "end": v(4.57, -7.57) * mm});
            skArc(sketch, "E19.0.1.144", {"start": v(3.57, -7.93) * mm, "mid": v(3.92, -7.93) * mm, "end": v(3.92, -7.57) * mm});
            skArc(sketch, "E19.0.1.145", {"start": v(-16.32, -7.93) * mm, "mid": v(-16.68, -7.92) * mm, "end": v(-16.68, -7.57) * mm});
            skArc(sketch, "E19.0.1.146", {"start": v(-13.43, -4.32) * mm, "mid": v(-13.07, -4.33) * mm, "end": v(-13.07, -4.68) * mm});
            skArc(sketch, "E19.0.1.147", {"start": v(-13.43, -7.93) * mm, "mid": v(-13.07, -7.92) * mm, "end": v(-13.07, -7.57) * mm});
            skLineSegment(sketch, "E19.direction1", {"start": v(-16.68, -12.43) * mm, "end": v(8.32, -12.43) * mm, "construction": true});
            skLineSegment(sketch, "E19.direction2", {"start": v(-16.68, -12.43) * mm, "end": v(-16.68, -7.92) * mm, "construction": true});
            skLineSegment(sketch, "E20.bottom", {"start": v(-13.38, 7.38) * mm, "end": v(-14.38, 7.38) * mm});
            skLineSegment(sketch, "E20.top", {"start": v(-13.38, 7.88) * mm, "end": v(-14.38, 7.88) * mm});
            skLineSegment(sketch, "E20.left", {"start": v(-13.38, 7.38) * mm, "end": v(-13.38, 7.88) * mm});
            skLineSegment(sketch, "E20.right", {"start": v(-14.38, 7.38) * mm, "end": v(-14.38, 7.88) * mm});
            skPoint(sketch, "E20.middle", {"position": v(-13.87, 7.63) * mm});
            skLineSegment(sketch, "E21.0.1.0", {"start": v(-14.38, -3.38) * mm, "end": v(-14.38, -2.87) * mm});
            skLineSegment(sketch, "E21.0.1.1", {"start": v(-13.38, -3.38) * mm, "end": v(-13.38, -2.87) * mm});
            skPoint(sketch, "E21.0.1.2", {"position": v(-13.87, -3.12) * mm});
            skLineSegment(sketch, "E21.0.1.3", {"start": v(-13.38, -3.37) * mm, "end": v(-14.38, -3.37) * mm});
            skLineSegment(sketch, "E21.0.1.4", {"start": v(-13.38, -2.87) * mm, "end": v(-14.38, -2.87) * mm});
            skLineSegment(sketch, "E21.1.0.0", {"start": v(-10.13, 7.38) * mm, "end": v(-10.13, 7.88) * mm});
            skLineSegment(sketch, "E21.1.0.1", {"start": v(-9.13, 7.38) * mm, "end": v(-9.13, 7.88) * mm});
            skPoint(sketch, "E21.1.0.2", {"position": v(-9.62, 7.63) * mm});
            skLineSegment(sketch, "E21.1.0.3", {"start": v(-9.13, 7.38) * mm, "end": v(-10.13, 7.38) * mm});
            skLineSegment(sketch, "E21.1.0.4", {"start": v(-9.13, 7.88) * mm, "end": v(-10.12, 7.88) * mm});
            skLineSegment(sketch, "E21.1.1.0", {"start": v(-10.13, -3.38) * mm, "end": v(-10.13, -2.88) * mm});
            skLineSegment(sketch, "E21.1.1.1", {"start": v(-9.13, -3.38) * mm, "end": v(-9.13, -2.88) * mm});
            skPoint(sketch, "E21.1.1.2", {"position": v(-9.62, -3.12) * mm});
            skLineSegment(sketch, "E21.1.1.3", {"start": v(-9.13, -3.37) * mm, "end": v(-10.13, -3.37) * mm});
            skLineSegment(sketch, "E21.1.1.4", {"start": v(-9.13, -2.87) * mm, "end": v(-10.12, -2.87) * mm});
            skLineSegment(sketch, "E21.2.0.0", {"start": v(-5.88, 7.38) * mm, "end": v(-5.88, 7.88) * mm});
            skLineSegment(sketch, "E21.2.0.1", {"start": v(-4.88, 7.38) * mm, "end": v(-4.88, 7.88) * mm});
            skPoint(sketch, "E21.2.0.2", {"position": v(-5.37, 7.63) * mm});
            skLineSegment(sketch, "E21.2.0.3", {"start": v(-4.88, 7.38) * mm, "end": v(-5.88, 7.38) * mm});
            skLineSegment(sketch, "E21.2.0.4", {"start": v(-4.88, 7.88) * mm, "end": v(-5.88, 7.88) * mm});
            skLineSegment(sketch, "E21.2.1.0", {"start": v(-5.88, -3.38) * mm, "end": v(-5.88, -2.88) * mm});
            skLineSegment(sketch, "E21.2.1.1", {"start": v(-4.88, -3.38) * mm, "end": v(-4.88, -2.88) * mm});
            skPoint(sketch, "E21.2.1.2", {"position": v(-5.37, -3.12) * mm});
            skLineSegment(sketch, "E21.2.1.3", {"start": v(-4.88, -3.37) * mm, "end": v(-5.88, -3.37) * mm});
            skLineSegment(sketch, "E21.2.1.4", {"start": v(-4.88, -2.87) * mm, "end": v(-5.88, -2.87) * mm});
            skLineSegment(sketch, "E21.3.0.0", {"start": v(-1.63, 7.38) * mm, "end": v(-1.63, 7.88) * mm});
            skLineSegment(sketch, "E21.3.0.1", {"start": v(-0.63, 7.38) * mm, "end": v(-0.63, 7.88) * mm});
            skPoint(sketch, "E21.3.0.2", {"position": v(-1.12, 7.63) * mm});
            skLineSegment(sketch, "E21.3.0.3", {"start": v(-0.63, 7.38) * mm, "end": v(-1.63, 7.38) * mm});
            skLineSegment(sketch, "E21.3.0.4", {"start": v(-0.63, 7.88) * mm, "end": v(-1.62, 7.88) * mm});
            skLineSegment(sketch, "E21.3.1.0", {"start": v(-1.63, -3.38) * mm, "end": v(-1.63, -2.88) * mm});
            skLineSegment(sketch, "E21.3.1.1", {"start": v(-0.63, -3.38) * mm, "end": v(-0.63, -2.88) * mm});
            skPoint(sketch, "E21.3.1.2", {"position": v(-1.12, -3.12) * mm});
            skLineSegment(sketch, "E21.3.1.3", {"start": v(-0.63, -3.37) * mm, "end": v(-1.63, -3.37) * mm});
            skLineSegment(sketch, "E21.3.1.4", {"start": v(-0.63, -2.87) * mm, "end": v(-1.62, -2.87) * mm});
            skLineSegment(sketch, "E21.4.0.0", {"start": v(2.62, 7.38) * mm, "end": v(2.62, 7.88) * mm});
            skLineSegment(sketch, "E21.4.0.1", {"start": v(3.62, 7.38) * mm, "end": v(3.62, 7.88) * mm});
            skPoint(sketch, "E21.4.0.2", {"position": v(3.13, 7.63) * mm});
            skLineSegment(sketch, "E21.4.0.3", {"start": v(3.62, 7.38) * mm, "end": v(2.62, 7.38) * mm});
            skLineSegment(sketch, "E21.4.0.4", {"start": v(3.62, 7.88) * mm, "end": v(2.63, 7.88) * mm});
            skLineSegment(sketch, "E21.4.1.0", {"start": v(2.62, -3.38) * mm, "end": v(2.62, -2.88) * mm});
            skLineSegment(sketch, "E21.4.1.1", {"start": v(3.62, -3.38) * mm, "end": v(3.62, -2.88) * mm});
            skPoint(sketch, "E21.4.1.2", {"position": v(3.13, -3.12) * mm});
            skLineSegment(sketch, "E21.4.1.3", {"start": v(3.62, -3.37) * mm, "end": v(2.62, -3.37) * mm});
            skLineSegment(sketch, "E21.4.1.4", {"start": v(3.62, -2.87) * mm, "end": v(2.63, -2.87) * mm});
            skLineSegment(sketch, "E21.5.0.0", {"start": v(6.87, 7.38) * mm, "end": v(6.87, 7.88) * mm});
            skLineSegment(sketch, "E21.5.0.1", {"start": v(7.88, 7.38) * mm, "end": v(7.88, 7.88) * mm});
            skPoint(sketch, "E21.5.0.2", {"position": v(7.38, 7.63) * mm});
            skLineSegment(sketch, "E21.5.0.3", {"start": v(7.88, 7.38) * mm, "end": v(6.87, 7.38) * mm});
            skLineSegment(sketch, "E21.5.0.4", {"start": v(7.87, 7.88) * mm, "end": v(6.88, 7.88) * mm});
            skLineSegment(sketch, "E21.5.1.0", {"start": v(6.87, -3.38) * mm, "end": v(6.87, -2.88) * mm});
            skLineSegment(sketch, "E21.5.1.1", {"start": v(7.88, -3.38) * mm, "end": v(7.88, -2.88) * mm});
            skPoint(sketch, "E21.5.1.2", {"position": v(7.38, -3.12) * mm});
            skLineSegment(sketch, "E21.5.1.3", {"start": v(7.88, -3.37) * mm, "end": v(6.87, -3.37) * mm});
            skLineSegment(sketch, "E21.5.1.4", {"start": v(7.87, -2.87) * mm, "end": v(6.88, -2.87) * mm});
            skLineSegment(sketch, "E21.6.0.0", {"start": v(11.12, 7.38) * mm, "end": v(11.12, 7.88) * mm});
            skLineSegment(sketch, "E21.6.0.1", {"start": v(12.12, 7.38) * mm, "end": v(12.12, 7.88) * mm});
            skPoint(sketch, "E21.6.0.2", {"position": v(11.63, 7.63) * mm});
            skLineSegment(sketch, "E21.6.0.3", {"start": v(12.12, 7.38) * mm, "end": v(11.12, 7.38) * mm});
            skLineSegment(sketch, "E21.6.0.4", {"start": v(12.12, 7.88) * mm, "end": v(11.12, 7.88) * mm});
            skLineSegment(sketch, "E21.6.1.0", {"start": v(11.12, -3.38) * mm, "end": v(11.12, -2.88) * mm});
            skLineSegment(sketch, "E21.6.1.1", {"start": v(12.12, -3.38) * mm, "end": v(12.12, -2.88) * mm});
            skPoint(sketch, "E21.6.1.2", {"position": v(11.63, -3.12) * mm});
            skLineSegment(sketch, "E21.6.1.3", {"start": v(12.12, -3.37) * mm, "end": v(11.12, -3.37) * mm});
            skLineSegment(sketch, "E21.6.1.4", {"start": v(12.12, -2.87) * mm, "end": v(11.12, -2.87) * mm});
            skLineSegment(sketch, "E21.7.0.0", {"start": v(15.38, 7.38) * mm, "end": v(15.38, 7.88) * mm});
            skLineSegment(sketch, "E21.7.0.1", {"start": v(16.38, 7.38) * mm, "end": v(16.38, 7.88) * mm});
            skPoint(sketch, "E21.7.0.2", {"position": v(15.88, 7.63) * mm});
            skLineSegment(sketch, "E21.7.0.3", {"start": v(16.38, 7.38) * mm, "end": v(15.38, 7.38) * mm});
            skLineSegment(sketch, "E21.7.0.4", {"start": v(16.38, 7.88) * mm, "end": v(15.38, 7.88) * mm});
            skLineSegment(sketch, "E21.7.1.0", {"start": v(15.38, -3.38) * mm, "end": v(15.38, -2.88) * mm});
            skLineSegment(sketch, "E21.7.1.1", {"start": v(16.38, -3.38) * mm, "end": v(16.38, -2.88) * mm});
            skPoint(sketch, "E21.7.1.2", {"position": v(15.88, -3.12) * mm});
            skLineSegment(sketch, "E21.7.1.3", {"start": v(16.38, -3.37) * mm, "end": v(15.38, -3.37) * mm});
            skLineSegment(sketch, "E21.7.1.4", {"start": v(16.38, -2.87) * mm, "end": v(15.38, -2.87) * mm});
            skLineSegment(sketch, "E21.direction1", {"start": v(-14.38, 7.38) * mm, "end": v(-10.13, 7.38) * mm, "construction": true});
            skLineSegment(sketch, "E21.direction2", {"start": v(-14.38, 7.38) * mm, "end": v(-14.38, -3.37) * mm, "construction": true});
            skLineSegment(sketch, "E22.bottom", {"start": v(-14.32, -14.13) * mm, "end": v(-15.32, -14.13) * mm});
            skLineSegment(sketch, "E22.top", {"start": v(-14.32, -13.63) * mm, "end": v(-15.32, -13.63) * mm});
            skLineSegment(sketch, "E22.left", {"start": v(-14.32, -14.13) * mm, "end": v(-14.32, -13.63) * mm});
            skLineSegment(sketch, "E22.right", {"start": v(-15.32, -14.13) * mm, "end": v(-15.32, -13.63) * mm});
            skPoint(sketch, "E22.middle", {"position": v(-14.82, -13.88) * mm});
            skLineSegment(sketch, "E23.1.0.0", {"start": v(-10.07, -14.13) * mm, "end": v(-10.07, -13.63) * mm});
            skLineSegment(sketch, "E23.1.0.1", {"start": v(-10.07, -13.63) * mm, "end": v(-11.07, -13.63) * mm});
            skLineSegment(sketch, "E23.1.0.2", {"start": v(-10.07, -14.13) * mm, "end": v(-11.07, -14.13) * mm});
            skLineSegment(sketch, "E23.1.0.3", {"start": v(-11.07, -14.13) * mm, "end": v(-11.07, -13.63) * mm});
            skPoint(sketch, "E23.1.0.4", {"position": v(-10.57, -13.88) * mm});
            skLineSegment(sketch, "E23.2.0.0", {"start": v(-5.82, -14.13) * mm, "end": v(-5.82, -13.63) * mm});
            skLineSegment(sketch, "E23.2.0.1", {"start": v(-5.82, -13.63) * mm, "end": v(-6.82, -13.63) * mm});
            skLineSegment(sketch, "E23.2.0.2", {"start": v(-5.82, -14.13) * mm, "end": v(-6.82, -14.13) * mm});
            skLineSegment(sketch, "E23.2.0.3", {"start": v(-6.82, -14.13) * mm, "end": v(-6.82, -13.63) * mm});
            skPoint(sketch, "E23.2.0.4", {"position": v(-6.32, -13.88) * mm});
            skLineSegment(sketch, "E23.3.0.0", {"start": v(-1.57, -14.13) * mm, "end": v(-1.57, -13.63) * mm});
            skLineSegment(sketch, "E23.3.0.1", {"start": v(-1.57, -13.63) * mm, "end": v(-2.57, -13.63) * mm});
            skLineSegment(sketch, "E23.3.0.2", {"start": v(-1.57, -14.13) * mm, "end": v(-2.57, -14.13) * mm});
            skLineSegment(sketch, "E23.3.0.3", {"start": v(-2.57, -14.13) * mm, "end": v(-2.57, -13.63) * mm});
            skPoint(sketch, "E23.3.0.4", {"position": v(-2.07, -13.88) * mm});
            skLineSegment(sketch, "E23.4.0.0", {"start": v(2.68, -14.13) * mm, "end": v(2.68, -13.63) * mm});
            skLineSegment(sketch, "E23.4.0.1", {"start": v(2.68, -13.63) * mm, "end": v(1.68, -13.63) * mm});
            skLineSegment(sketch, "E23.4.0.2", {"start": v(2.68, -14.13) * mm, "end": v(1.68, -14.13) * mm});
            skLineSegment(sketch, "E23.4.0.3", {"start": v(1.68, -14.13) * mm, "end": v(1.68, -13.63) * mm});
            skPoint(sketch, "E23.4.0.4", {"position": v(2.18, -13.88) * mm});
            skLineSegment(sketch, "E23.5.0.0", {"start": v(6.93, -14.13) * mm, "end": v(6.93, -13.63) * mm});
            skLineSegment(sketch, "E23.5.0.1", {"start": v(6.93, -13.63) * mm, "end": v(5.93, -13.63) * mm});
            skLineSegment(sketch, "E23.5.0.2", {"start": v(6.93, -14.13) * mm, "end": v(5.93, -14.13) * mm});
            skLineSegment(sketch, "E23.5.0.3", {"start": v(5.93, -14.13) * mm, "end": v(5.93, -13.63) * mm});
            skPoint(sketch, "E23.5.0.4", {"position": v(6.43, -13.88) * mm});
            skLineSegment(sketch, "E23.6.0.0", {"start": v(11.18, -14.13) * mm, "end": v(11.18, -13.63) * mm});
            skLineSegment(sketch, "E23.6.0.1", {"start": v(11.18, -13.63) * mm, "end": v(10.18, -13.63) * mm});
            skLineSegment(sketch, "E23.6.0.2", {"start": v(11.18, -14.13) * mm, "end": v(10.18, -14.13) * mm});
            skLineSegment(sketch, "E23.6.0.3", {"start": v(10.18, -14.13) * mm, "end": v(10.18, -13.63) * mm});
            skPoint(sketch, "E23.6.0.4", {"position": v(10.68, -13.88) * mm});
            skLineSegment(sketch, "E23.7.0.0", {"start": v(15.43, -14.13) * mm, "end": v(15.43, -13.63) * mm});
            skLineSegment(sketch, "E23.7.0.1", {"start": v(15.43, -13.63) * mm, "end": v(14.43, -13.63) * mm});
            skLineSegment(sketch, "E23.7.0.2", {"start": v(15.43, -14.13) * mm, "end": v(14.43, -14.13) * mm});
            skLineSegment(sketch, "E23.7.0.3", {"start": v(14.43, -14.13) * mm, "end": v(14.43, -13.63) * mm});
            skPoint(sketch, "E23.7.0.4", {"position": v(14.93, -13.88) * mm});
            skLineSegment(sketch, "E23.direction1", {"start": v(-15.32, -14.13) * mm, "end": v(-11.07, -14.13) * mm, "construction": true});
            skLineSegment(sketch, "E24.bottom", {"start": v(22.5, -15.62) * mm, "end": v(-22.5, -15.63) * mm});
            skLineSegment(sketch, "E24.top", {"start": v(22.5, 15.63) * mm, "end": v(-22.5, 15.62) * mm});
            skLineSegment(sketch, "E24.left", {"start": v(22.5, -15.62) * mm, "end": v(22.5, 15.63) * mm});
            skLineSegment(sketch, "E24.right", {"start": v(-22.5, -15.63) * mm, "end": v(-22.5, 15.62) * mm});
            skPoint(sketch, "E24.middle", {"position": v(0, 0) * mm});
            skLineSegment(sketch, "E25.bottom", {"start": v(18.7, -5) * mm, "end": v(19.3, -5) * mm});
            skLineSegment(sketch, "E25.top", {"start": v(18.7, 5) * mm, "end": v(19.3, 5) * mm});
            skLineSegment(sketch, "E25.left", {"start": v(18.7, -5) * mm, "end": v(18.7, 5) * mm});
            skLineSegment(sketch, "E25.right", {"start": v(19.3, -5) * mm, "end": v(19.3, 5) * mm});
            skPoint(sketch, "E25.middle", {"position": v(19, 0) * mm});
            skPoint(sketch, "E25.middle.positionSnap0", {"position": v(22.5, 0) * mm});
            skPoint(sketch, "E25.centerSnap0", {"position": v(22.5, 0) * mm});
            skLineSegment(sketch, "E26.MirrorCS", {"start": v(-18.7, -5) * mm, "end": v(-19.3, -5) * mm});
            skLineSegment(sketch, "E27.MirrorCS", {"start": v(-18.7, 5) * mm, "end": v(-19.3, 5) * mm});
            skLineSegment(sketch, "E28.MirrorCS", {"start": v(-18.7, -5) * mm, "end": v(-18.7, 5) * mm});
            skLineSegment(sketch, "E29.MirrorCS", {"start": v(-19.3, -5) * mm, "end": v(-19.3, 5) * mm});
            skPoint(sketch, "E30.MirrorP", {"position": v(-19, 0) * mm});
            skSolve(sketch);
        }
        {
            var Q0;
            Q0=makeQuery(id+"F0.imprint","IMPRINT",FACE,{"disambiguationData":[TD([[makeQuery(id+"F0.imprint","IMPRINT",EDGE,{"derivedFrom":sQuery(id+"F0.wireOp",EDGE,"E0.bottom")}),1.0]])]});
            var Q1;
            Q1=makeQuery(id+"F0.imprint","IMPRINT",FACE,{"disambiguationData":[TD([[makeQuery(id+"F0.imprint","IMPRINT",EDGE,{"derivedFrom":sQuery(id+"F0.wireOp",EDGE,"E15.MirrorC")}),-1.0]])]});
            var Q2;
            Q2=makeQuery(id+"F0.imprint","IMPRINT",FACE,{"disambiguationData":[TD([[makeQuery(id+"F0.imprint","IMPRINT",EDGE,{"derivedFrom":sQuery(id+"F0.wireOp",EDGE,"E17.MirrorC")}),1.0]])]});
            var Q3;
            Q3=makeQuery(id+"F0.imprint","IMPRINT",FACE,{"disambiguationData":[TD([[makeQuery(id+"F0.imprint","IMPRINT",EDGE,{"derivedFrom":sQuery(id+"F0.wireOp",EDGE,"E16.MirrorC")}),-1.0]])]});
            var Q4;
            Q4=makeQuery(id+"F0.imprint","IMPRINT",FACE,{"disambiguationData":[TD([[makeQuery(id+"F0.imprint","IMPRINT",EDGE,{"derivedFrom":sQuery(id+"F0.wireOp",EDGE,"E14")}),1.0]])]});
            var Q5;
            Q5=makeQuery(id+"F0.imprint","IMPRINT",FACE,{"disambiguationData":[TD([[makeQuery(id+"F0.imprint","IMPRINT",EDGE,{"derivedFrom":sQuery(id+"F0.wireOp",EDGE,"E25.bottom")}),1.0]])]});
            var Q6;
            Q6=makeQuery(id+"F0.imprint","IMPRINT",FACE,{"disambiguationData":[TD([[makeQuery(id+"F0.imprint","IMPRINT",EDGE,{"derivedFrom":sQuery(id+"F0.wireOp",EDGE,"E26.MirrorCS")}),-1.0]])]});
            extrude(context, id + "F1", {"entities" : qUnion([Q0, Q1, Q2, Q3, Q4, Q5, Q6]), "depth" : 0.6 * mm});
        }
        {
            var Q0;
            Q0=makeQuery(id+"F0.imprint","IMPRINT",FACE,{"disambiguationData":[TD([[makeQuery(id+"F0.imprint","IMPRINT",EDGE,{"derivedFrom":sQuery(id+"F0.wireOp",EDGE,"E14")}),1.0]])]});
            var Q1;
            Q1=makeQuery(id+"F0.imprint","IMPRINT",FACE,{"disambiguationData":[TD([[makeQuery(id+"F0.imprint","IMPRINT",EDGE,{"derivedFrom":sQuery(id+"F0.wireOp",EDGE,"E16.MirrorC")}),-1.0]])]});
            var Q2;
            Q2=makeQuery(id+"F0.imprint","IMPRINT",FACE,{"disambiguationData":[TD([[makeQuery(id+"F0.imprint","IMPRINT",EDGE,{"derivedFrom":sQuery(id+"F0.wireOp",EDGE,"E17.MirrorC")}),1.0]])]});
            var Q3;
            Q3=makeQuery(id+"F0.imprint","IMPRINT",FACE,{"disambiguationData":[TD([[makeQuery(id+"F0.imprint","IMPRINT",EDGE,{"derivedFrom":sQuery(id+"F0.wireOp",EDGE,"E15.MirrorC")}),-1.0]])]});
            extrude(context, id + "F2", {"entities" : qUnion([Q0, Q1, Q2, Q3]), "operationType" : NewBodyOperationType.ADD, "oppositeDirection" : true, "depth" : 1 * mm});
        }
        {
            var Q0;
            Q0=makeQuery(id+"F0.imprint","IMPRINT",FACE,{"disambiguationData":[TD([[makeQuery(id+"F0.imprint","IMPRINT",EDGE,{"derivedFrom":sQuery(id+"F0.wireOp",EDGE,"E26.MirrorCS")}),-1.0]])]});
            var Q1;
            Q1=makeQuery(id+"F0.imprint","IMPRINT",FACE,{"disambiguationData":[TD([[makeQuery(id+"F0.imprint","IMPRINT",EDGE,{"derivedFrom":sQuery(id+"F0.wireOp",EDGE,"E25.bottom")}),1.0]])]});
            extrude(context, id + "F3", {"entities" : qUnion([Q0, Q1]), "operationType" : NewBodyOperationType.ADD, "oppositeDirection" : true, "depth" : 0.2 * mm});
        }
    });
